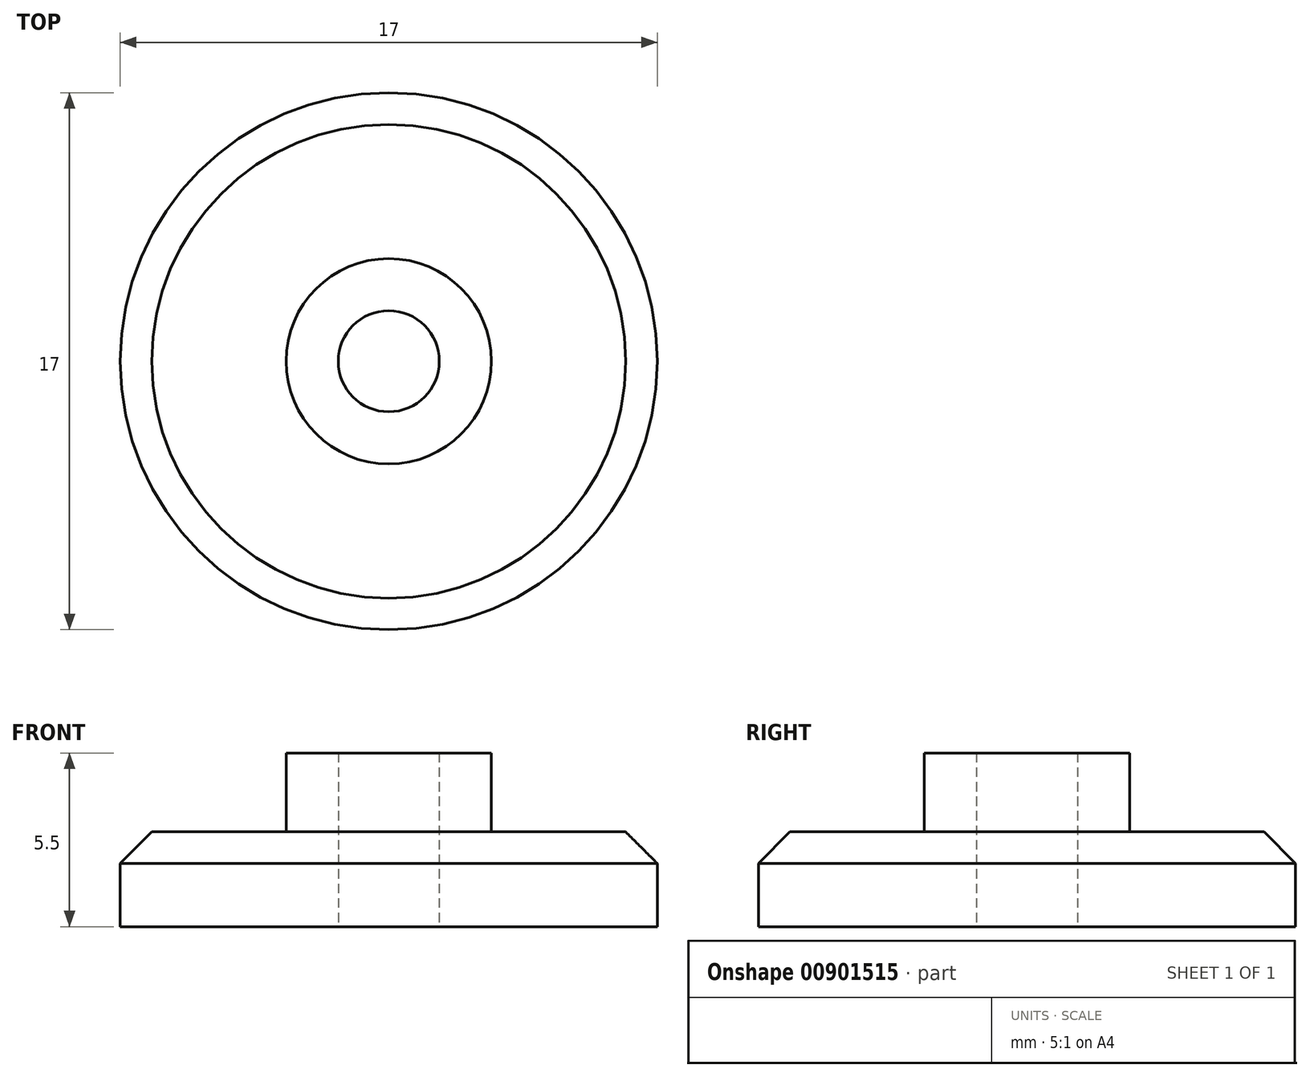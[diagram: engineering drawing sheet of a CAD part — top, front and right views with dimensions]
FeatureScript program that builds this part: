
annotation { "Feature Type Name" : "Feature", "Feature Type Description" : "" }
export const myFeature = defineFeature(function(context is Context, id is Id, definition is map)
    precondition{}
    {
        {
            var Q0;
            Q0=qCreatedBy(makeId("Top.planeOp"),FACE);
            var sketch = newSketch(context, id + "F0", { "sketchPlane" : qUnion([Q0])});
            skCircle(sketch, "E0", {"center": v(0, 0) * mm, "radius": 8.5 * mm});
            skSolve(sketch);
        }
        {
            var Q0;
            Q0=makeQuery(id+"F0.imprint","IMPRINT",FACE,{"disambiguationData":[TD([[makeQuery(id+"F0.imprint","IMPRINT",EDGE,{"derivedFrom":sQuery(id+"F0.wireOp",EDGE,"E0")}),1.0]])]});
            extrude(context, id + "F1", {"entities" : qUnion([Q0]), "depth" : 3 * mm, "offsetDistance" : 25 * mm});
        }
        {
            var Q0;
            Q0=makeQuery(id+"F1.opExtrude","CAP_EDGE",EDGE,{"disambiguationData":[OSD([sQuery(id+"F0.wireOp",EDGE,"E0")])],"isStart":false});
            chamfer(context, id + "F2", {"entities" : qUnion([Q0]), "width" : 1 * mm, "tangentPropagation" : true});
        }
        {
            var Q0;
            Q0=sQuery(id+"F0.wireOp",VERTEX,"E0.center");
            var Q1;
            Q1=makeQuery(id+"F1.opExtrude","SWEPT_BODY",BODY,{"disambiguationData":[OSD([sQuery(id+"F0.wireOp",EDGE,"E0")])]});
            hole(context, id + "F3", {"style" : HoleStyle.SIMPLE, "endStyle" : HoleEndStyle.THROUGH, "oppositeDirection" : true, "holeDiameter" : 3.2 * mm, "majorDiameter" : 5 * mm, "isTappedThrough" : true, "tappedDepth" : 12 * mm, "tapClearance" : 3, "locations" : qUnion([Q0]), "scope" : qUnion([Q1])});
        }
        {
            var Q0;
            Q0=makeQuery(id+"F1.opExtrude","CAP_FACE",FACE,{"disambiguationData":[OSD([sQuery(id+"F0.wireOp",EDGE,"E0")])],"isStart":false});
            var sketch = newSketch(context, id + "F4", { "sketchPlane" : qUnion([Q0])});
            skPoint(sketch, "E1", {"position": v(0, 0) * mm});
            skCircle(sketch, "E2", {"center": v(0, 0) * mm, "radius": 3.25 * mm});
            skSolve(sketch);
        }
        {
            var Q0;
            Q0=makeQuery(id+"F4.imprint","IMPRINT",FACE,{"disambiguationData":[TD([[makeQuery(id+"F4.imprint","IMPRINT",EDGE,{"derivedFrom":sQuery(id+"F4.wireOp",EDGE,"E2")}),1.0]])]});
            extrude(context, id + "F5", {"entities" : qUnion([Q0]), "operationType" : NewBodyOperationType.ADD, "depth" : 2.5 * mm, "offsetDistance" : 25 * mm});
        }
    });
